# Revit family: spectral_norea_norea-a_1545_11250_840_mps_97e0
name_source: partatom
category: Lighting Fixtures
revit_build: Autodesk Revit 2016 (Build: 20150220_1215(x64)
units: mm (PartAtom-declared; Revit-internal decimal feet)

## family parameters
Cut with Voids When Loaded = No
Host = Face
Light Source = No
Part Type = Normal
Room Calculation Point = No
Round Connector Dimension = Use Diameter
Shared = No

## types (1)
- SPECTRAL NOREA (1 x )
    Apparent Load = 0 VA
    Approval mark = CE
    CIE Flux Codes = 64 90 97 96 73
    Control Gear = Electronic transformer
    Default Elevation = 1800 mm
    Description = SPT0000089
NOREA surface-mounted luminaire 

Design:
Rectangular luminaire element with a microprism panel in a natural anodised aluminium profile frame surround. The frame can be removed using a bayonet
fixture. The LED module is formed as a square LED flat board and screwed to the luminaire element. For connection of the luminaire this can be hinged
down and fastened with screws at an oblong hole in the powder-coated metal body. The indirect component is ensured by recesses in the top of the metal
body. The metal body accommodates the electrical components and electronic ballast. Luminaire with heat-resistant wiring. Variant suitable for office use with a microprism panel MPS. The LED points are visible as circles on the microprism panel. Suitable for ceiling or wall mounting. Also in a dimmable version. Protection rating IP20, safety class I.

Colour:
Housing – similar to RAL 9016 White silk matt;
Frame – natural anodised
    Height = 50 mm
    Lamp = 1 x
    Lamp count = 1
    Length = 1545 mm
    Luminous efficacy = 0 lm/W
    Manufacturer = Ridi
    ModVariant = No
    Model = NOREA-A 1545/11250/840 MPS
    Mounting Place = Ceiling
    Mounting Type = Surface mounted
    Number of Poles = 1
    OnlyDefault = Yes
    Power Factor = 1
    Product Name = SPECTRAL NOREA
    Product group = Ceiling mounted luminaire
    ProductGroupID = 3
    Protection Class = Protection class
    Protection Degree = IP 20
    RlxData = <blob elided: 44157 chars, md5=552a5581>
    Socket = socket
    Standby Power = 0 W
    System Light Flux = 0 lm
    System Power = 0 W
    Type Image = elementary02.jpg
    URL = http://reluxnet.relux.com
    VarID = 1
    Voltage = 0 V
    Weight = 0.00 kg
    Width = 312 mm

## geometry (parser evidence)
native form markers: Blend x4, Sweep x9
no freeform markers — native parametric forms only
